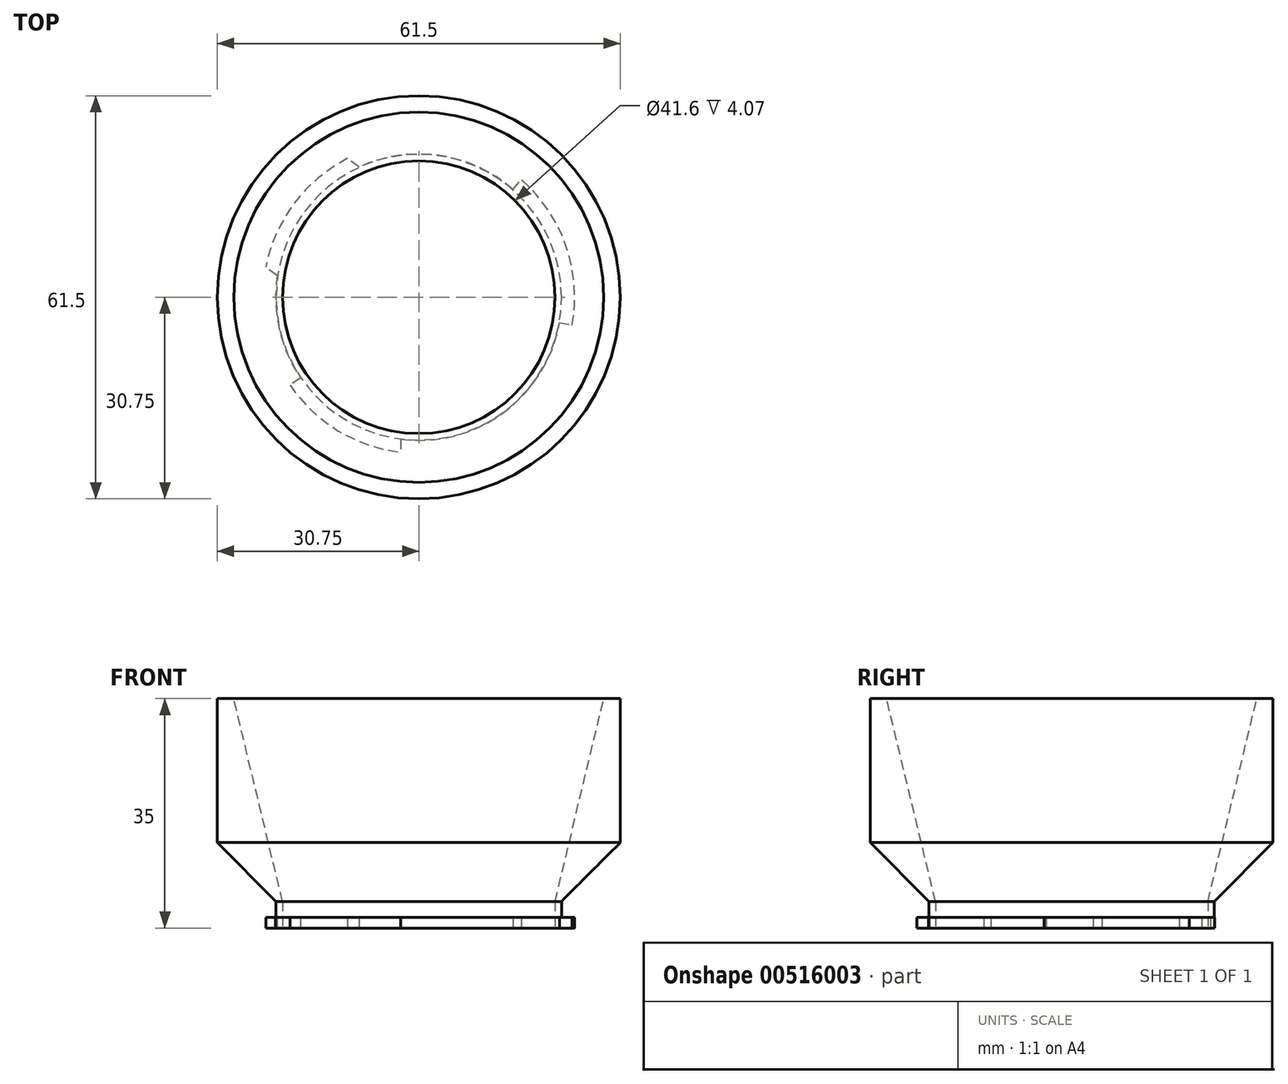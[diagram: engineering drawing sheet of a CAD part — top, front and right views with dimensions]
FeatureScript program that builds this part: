
annotation { "Feature Type Name" : "Feature", "Feature Type Description" : "" }
export const myFeature = defineFeature(function(context is Context, id is Id, definition is map)
    precondition{}
    {
        {
            var Q0;
            Q0=qCreatedBy(makeId("Top.planeOp"),FACE);
            var sketch = newSketch(context, id + "F0", { "sketchPlane" : qUnion([Q0])});
            skCircle(sketch, "E0", {"center": v(0, 0) * mm, "radius": 20.8 * mm});
            skArc(sketch, "E1", {"start": v(-21.6, 3.3) * mm, "mid": v(-21.3, -4.85) * mm, "end": v(-18.04, -12.33) * mm});
            skArc(sketch, "E2", {"start": v(-10.87, 21.18) * mm, "mid": v(-19, 14.33) * mm, "end": v(-23.35, 4.62) * mm});
            skPoint(sketch, "E3", {"position": v(-9.12, 19.86) * mm});
            skPoint(sketch, "E4", {"position": v(14.37, 16.46) * mm});
            skPoint(sketch, "E5", {"position": v(21.5, -3.88) * mm});
            skPoint(sketch, "E6", {"position": v(-2.78, -21.67) * mm});
            skPoint(sketch, "E7", {"position": v(-18.04, -12.33) * mm});
            skPoint(sketch, "E8", {"position": v(-21.6, 3.3) * mm});
            skLineSegment(sketch, "E9", {"start": v(-9.12, 19.86) * mm, "end": v(-21.6, 3.3) * mm, "construction": true});
            skLineSegment(sketch, "E10", {"start": v(-21.6, 3.3) * mm, "end": v(-22.88, -5.04) * mm, "construction": true});
            skLineSegment(sketch, "E11", {"start": v(-21.6, 3.3) * mm, "end": v(-23.35, 4.62) * mm});
            skLineSegment(sketch, "E12", {"start": v(-9.12, 19.86) * mm, "end": v(-0.54, 23.8) * mm, "construction": true});
            skLineSegment(sketch, "E13", {"start": v(14.37, 16.46) * mm, "end": v(21.5, -3.88) * mm, "construction": true});
            skLineSegment(sketch, "E14", {"start": v(14.37, 16.46) * mm, "end": v(8.84, 21.29) * mm, "construction": true});
            skLineSegment(sketch, "E15", {"start": v(14.37, 16.46) * mm, "end": v(15.65, 17.93) * mm});
            skLineSegment(sketch, "E16", {"start": v(21.5, -3.88) * mm, "end": v(20, -12.24) * mm, "construction": true});
            skLineSegment(sketch, "E17", {"start": v(21.5, -3.88) * mm, "end": v(23.42, -4.23) * mm});
            skLineSegment(sketch, "E18", {"start": v(-2.78, -21.67) * mm, "end": v(4.8, -22.65) * mm, "construction": true});
            skLineSegment(sketch, "E19", {"start": v(-2.78, -21.67) * mm, "end": v(-2.78, -23.64) * mm});
            skLineSegment(sketch, "E20", {"start": v(-18.04, -12.33) * mm, "end": v(-21.8, -6.84) * mm, "construction": true});
            skLineSegment(sketch, "E21", {"start": v(-18.04, -12.33) * mm, "end": v(-19.65, -13.43) * mm});
            skLineSegment(sketch, "E22", {"start": v(-9.12, 19.86) * mm, "end": v(-10.87, 21.18) * mm});
            skArc(sketch, "E23.trimOffspring", {"start": v(23.42, -4.23) * mm, "mid": v(22.46, 7.87) * mm, "end": v(15.65, 17.93) * mm});
            skArc(sketch, "E24.trimOffspring", {"start": v(-19.65, -13.43) * mm, "mid": v(-12.32, -20.36) * mm, "end": v(-2.78, -23.64) * mm});
            skArc(sketch, "E25.trimOffspring", {"start": v(-2.78, -21.67) * mm, "mid": v(12.91, -17.63) * mm, "end": v(21.5, -3.88) * mm});
            skArc(sketch, "E26.trimOffspring", {"start": v(14.37, 16.46) * mm, "mid": v(3.13, 21.63) * mm, "end": v(-9.12, 19.86) * mm});
            skSolve(sketch);
        }
        {
            var Q0;
            Q0=makeQuery(id+"F0.imprint","IMPRINT",FACE,{"disambiguationData":[TD([[makeQuery(id+"F0.imprint","IMPRINT",EDGE,{"derivedFrom":sQuery(id+"F0.wireOp",EDGE,"E0")}),-1.0]])]});
            extrude(context, id + "F1", {"entities" : qUnion([Q0]), "depth" : 1.65 * mm, "offsetDistance" : 25.4 * mm});
        }
        {
            var Q0;
            Q0=makeQuery(id+"F1.opExtrude","CAP_FACE",FACE,{"disambiguationData":[OSD([sQuery(id+"F0.wireOp",EDGE,"E0"),sQuery(id+"F0.wireOp",EDGE,"E1"),sQuery(id+"F0.wireOp",EDGE,"E2"),sQuery(id+"F0.wireOp",EDGE,"E11"),sQuery(id+"F0.wireOp",EDGE,"E15"),sQuery(id+"F0.wireOp",EDGE,"E17"),sQuery(id+"F0.wireOp",EDGE,"E19"),sQuery(id+"F0.wireOp",EDGE,"E21"),sQuery(id+"F0.wireOp",EDGE,"E22"),sQuery(id+"F0.wireOp",EDGE,"E23.trimOffspring"),sQuery(id+"F0.wireOp",EDGE,"E24.trimOffspring"),sQuery(id+"F0.wireOp",EDGE,"E25.trimOffspring"),sQuery(id+"F0.wireOp",EDGE,"E26.trimOffspring")])],"isStart":false});
            var sketch = newSketch(context, id + "F2", { "sketchPlane" : qUnion([Q0])});
            skCircle(sketch, "E27", {"center": v(0, 0) * mm, "radius": 21.79 * mm});
            skCircle(sketch, "E28.0", {"center": v(0, 0) * mm, "radius": 20.8 * mm});
            skSolve(sketch);
        }
        {
            var Q0;
            Q0=makeQuery(id+"F2.imprint","IMPRINT",FACE,{"disambiguationData":[TD([[makeQuery(id+"F2.imprint","IMPRINT",EDGE,{"derivedFrom":sQuery(id+"F2.wireOp",EDGE,"E27")}),1.0]])]});
            extrude(context, id + "F3", {"entities" : qUnion([Q0]), "operationType" : NewBodyOperationType.ADD, "depth" : 4.07 * mm - 1.65 * mm, "offsetDistance" : 25.4 * mm});
        }
        {
            var Q0;
            Q0=qCreatedBy(makeId("Right.planeOp"),FACE);
            var sketch = newSketch(context, id + "F4", { "sketchPlane" : qUnion([Q0])});
            skLineSegment(sketch, "E29", {"start": v(0, 0) * mm, "end": v(0, 35) * mm, "construction": true});
            skLineSegment(sketch, "E30", {"start": v(-30.75, 35) * mm, "end": v(30.75, 35) * mm, "construction": true});
            skLineSegment(sketch, "E31.0", {"start": v(-20.8, 4.07) * mm, "end": v(20.8, 4.07) * mm, "construction": true});
            skLineSegment(sketch, "E32", {"start": v(-20.8, 4.07) * mm, "end": v(-28.25, 35) * mm});
            skLineSegment(sketch, "E33", {"start": v(-28.25, 35) * mm, "end": v(-30.75, 35) * mm});
            skLineSegment(sketch, "E34", {"start": v(-21.79, 4.07) * mm, "end": v(-20.8, 4.07) * mm});
            skLineSegment(sketch, "E35", {"start": v(-30.75, 35) * mm, "end": v(-30.75, 13.03) * mm});
            skLineSegment(sketch, "E36", {"start": v(-30.75, 13.03) * mm, "end": v(-21.8, 4.07) * mm});
            skSolve(sketch);
        }
        {
            var Q0;
            Q0=makeQuery(id+"F4.imprint","IMPRINT",FACE,{"disambiguationData":[TD([[makeQuery(id+"F4.imprint","IMPRINT",EDGE,{"derivedFrom":sQuery(id+"F4.wireOp",EDGE,"KpQdQwXl-EACe-sCyQ-Q2DE-3IYzWhqLDo4g")}),-1.0]])]});
            var Q1;
            Q1=makeQuery(id+"F4.imprint","IMPRINT",FACE,{"disambiguationData":[TD([[makeQuery(id+"F4.imprint","IMPRINT",EDGE,{"derivedFrom":sQuery(id+"F4.wireOp",EDGE,"E32")}),1.0]])]});
            var Q2;
            Q2=sQuery(id+"F4.wireOp",EDGE,"E29");
            revolve(context, id + "F5", {"operationType" : NewBodyOperationType.ADD, "entities" : qUnion([Q0, Q1]), "axis" : qUnion([Q2]), "revolveType" : RevolveType.FULL});
        }
    });
